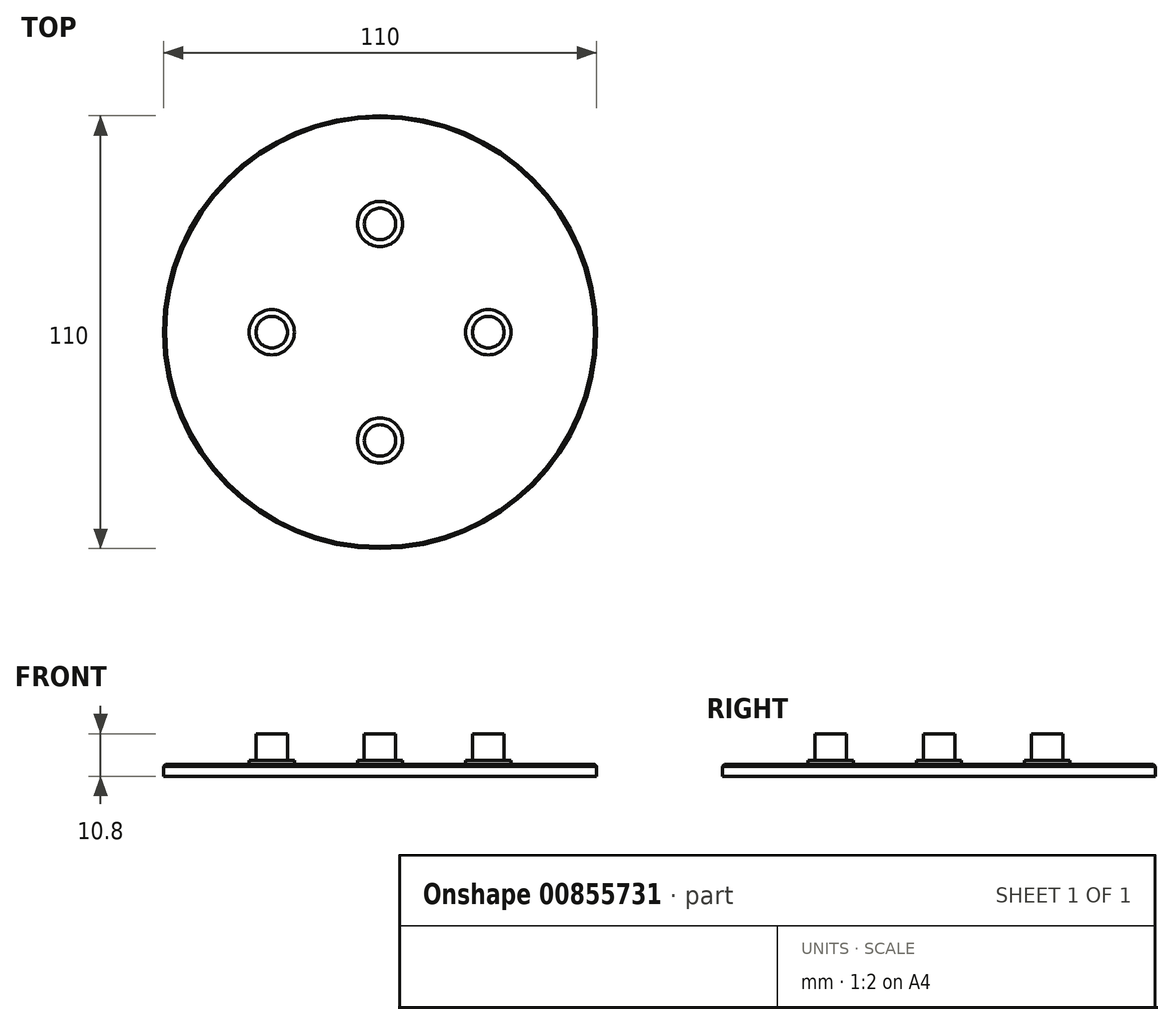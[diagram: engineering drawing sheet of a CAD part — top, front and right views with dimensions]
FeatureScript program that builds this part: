
annotation { "Feature Type Name" : "Feature", "Feature Type Description" : "" }
export const myFeature = defineFeature(function(context is Context, id is Id, definition is map)
    precondition{}
    {
        {
            var Q0;
            Q0=qCreatedBy(makeId("Top.planeOp"),FACE);
            var sketch = newSketch(context, id + "F0", { "sketchPlane" : qUnion([Q0])});
            skCircle(sketch, "E0", {"center": v(0, 0) * mm, "radius": 55 * mm});
            skSolve(sketch);
        }
        {
            var Q0;
            Q0 = qSketchRegion(id + "F0", true);
            extrude(context, id + "F1", {"entities" : qUnion([Q0]), "depth" : 3 * mm, "offsetDistance" : 25 * mm});
        }
        {
            var Q0;
            Q0=makeQuery(id+"F1.opExtrude","CAP_FACE",FACE,{"disambiguationData":[OSD([sQuery(id+"F0.wireOp",EDGE,"E0")])],"isStart":false});
            var sketch = newSketch(context, id + "F2", { "sketchPlane" : qUnion([Q0])});
            skCircle(sketch, "E1", {"center": v(-27.5, 0) * mm, "radius": 5.75 * mm});
            skCircle(sketch, "E2", {"center": v(27.5, 0) * mm, "radius": 5.75 * mm});
            skCircle(sketch, "E3", {"center": v(0, 27.5) * mm, "radius": 5.75 * mm});
            skCircle(sketch, "E4", {"center": v(0, -27.5) * mm, "radius": 5.75 * mm});
            skSolve(sketch);
        }
        {
            var Q0;
            Q0 = qSketchRegion(id + "F2", true);
            extrude(context, id + "F3", {"entities" : qUnion([Q0]), "operationType" : NewBodyOperationType.ADD, "depth" : 1 * mm, "offsetDistance" : 25 * mm});
        }
        {
            var Q0;
            Q0=makeQuery(id+"F3.opExtrude","CAP_FACE",FACE,{"disambiguationData":[OSD([sQuery(id+"F2.wireOp",EDGE,"E1")])],"isStart":false});
            var sketch = newSketch(context, id + "F4", { "sketchPlane" : qUnion([Q0])});
            skCircle(sketch, "E5", {"center": v(-27.5, 0) * mm, "radius": 4 * mm});
            skSolve(sketch);
        }
        {
            var Q0;
            Q0=makeQuery(id+"F3.opExtrude","CAP_FACE",FACE,{"disambiguationData":[OSD([sQuery(id+"F2.wireOp",EDGE,"E2")])],"isStart":false});
            var sketch = newSketch(context, id + "F5", { "sketchPlane" : qUnion([Q0])});
            skCircle(sketch, "E6", {"center": v(27.5, 0) * mm, "radius": 4 * mm});
            skSolve(sketch);
        }
        {
            var Q0;
            Q0 = qSketchRegion(id + "F5", true);
            extrude(context, id + "F6", {"entities" : qUnion([Q0]), "operationType" : NewBodyOperationType.ADD, "depth" : 6.8 * mm, "offsetDistance" : 25 * mm});
        }
        {
            var Q0;
            Q0 = qSketchRegion(id + "F4", true);
            extrude(context, id + "F7", {"entities" : qUnion([Q0]), "operationType" : NewBodyOperationType.ADD, "depth" : 6.8 * mm, "offsetDistance" : 25 * mm});
        }
        {
            var Q0;
            Q0=makeQuery(id+"F3.opExtrude","CAP_FACE",FACE,{"disambiguationData":[OSD([sQuery(id+"F2.wireOp",EDGE,"E3")])],"isStart":false});
            var sketch = newSketch(context, id + "F8", { "sketchPlane" : qUnion([Q0])});
            skCircle(sketch, "E7", {"center": v(0, 27.5) * mm, "radius": 4 * mm});
            skSolve(sketch);
        }
        {
            var Q0;
            Q0 = qSketchRegion(id + "F8", true);
            extrude(context, id + "F9", {"entities" : qUnion([Q0]), "operationType" : NewBodyOperationType.ADD, "depth" : 6.8 * mm, "offsetDistance" : 25 * mm});
        }
        {
            var Q0;
            Q0=makeQuery(id+"F3.opExtrude","CAP_FACE",FACE,{"disambiguationData":[OSD([sQuery(id+"F2.wireOp",EDGE,"E4")])],"isStart":false});
            var sketch = newSketch(context, id + "F10", { "sketchPlane" : qUnion([Q0])});
            skCircle(sketch, "E8", {"center": v(0, -27.5) * mm, "radius": 4 * mm});
            skSolve(sketch);
        }
        {
            var Q0;
            Q0 = qSketchRegion(id + "F10", true);
            extrude(context, id + "F11", {"entities" : qUnion([Q0]), "operationType" : NewBodyOperationType.ADD, "depth" : 6.8 * mm, "offsetDistance" : 25 * mm});
        }
        {
            var Q0;
            Q0=makeQuery(id+"F1.opExtrude","CAP_EDGE",EDGE,{"disambiguationData":[OSD([sQuery(id+"F0.wireOp",EDGE,"E0")])],"isStart":false});
            chamfer(context, id + "F12", {"entities" : qUnion([Q0]), "width" : .5 * mm, "tangentPropagation" : true});
        }
    });
